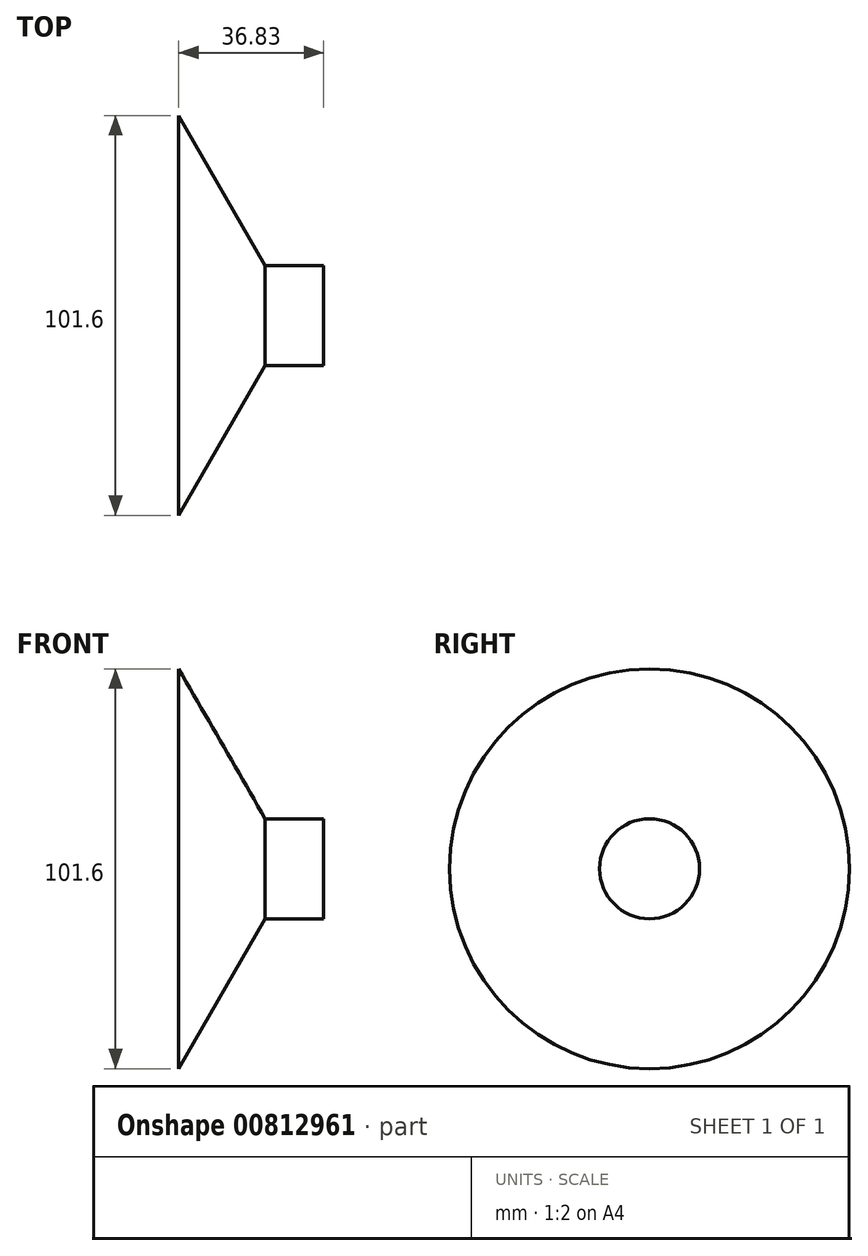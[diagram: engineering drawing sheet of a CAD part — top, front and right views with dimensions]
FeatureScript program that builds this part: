
annotation { "Feature Type Name" : "Feature", "Feature Type Description" : "" }
export const myFeature = defineFeature(function(context is Context, id is Id, definition is map)
    precondition{}
    {
        {
            var Q0;
            Q0=qCreatedBy(makeId("Front.planeOp"),FACE);
            var sketch = newSketch(context, id + "F0", { "sketchPlane" : qUnion([Q0])});
            skLineSegment(sketch, "E0", {"start": v(-493.5, 0) * mm, "end": v(576.48, 0) * mm, "construction": true});
            skLineSegment(sketch, "E1", {"start": v(-14.75, 0) * mm, "end": v(-14.75, 50.8) * mm});
            skLineSegment(sketch, "E2", {"start": v(-14.75, 50.8) * mm, "end": v(7.25, 12.7) * mm});
            skLineSegment(sketch, "E3", {"start": v(7.25, 12.7) * mm, "end": v(22.08, 12.7) * mm});
            skLineSegment(sketch, "E4", {"start": v(22.08, 12.7) * mm, "end": v(22.08, 0) * mm});
            skLineSegment(sketch, "E5", {"start": v(22.08, 0) * mm, "end": v(-14.75, 0) * mm});
            skSolve(sketch);
        }
        {
            var Q0;
            Q0 = qSketchRegion(id + "F0", true);
            var Q1;
            Q1=sQuery(id+"F0.wireOp",EDGE,"E0");
            revolve(context, id + "F1", {"surfaceOperationType" : NewSurfaceOperationType.NEW, "entities" : qUnion([Q0]), "axis" : qUnion([Q1]), "revolveType" : RevolveType.FULL});
        }
    });
